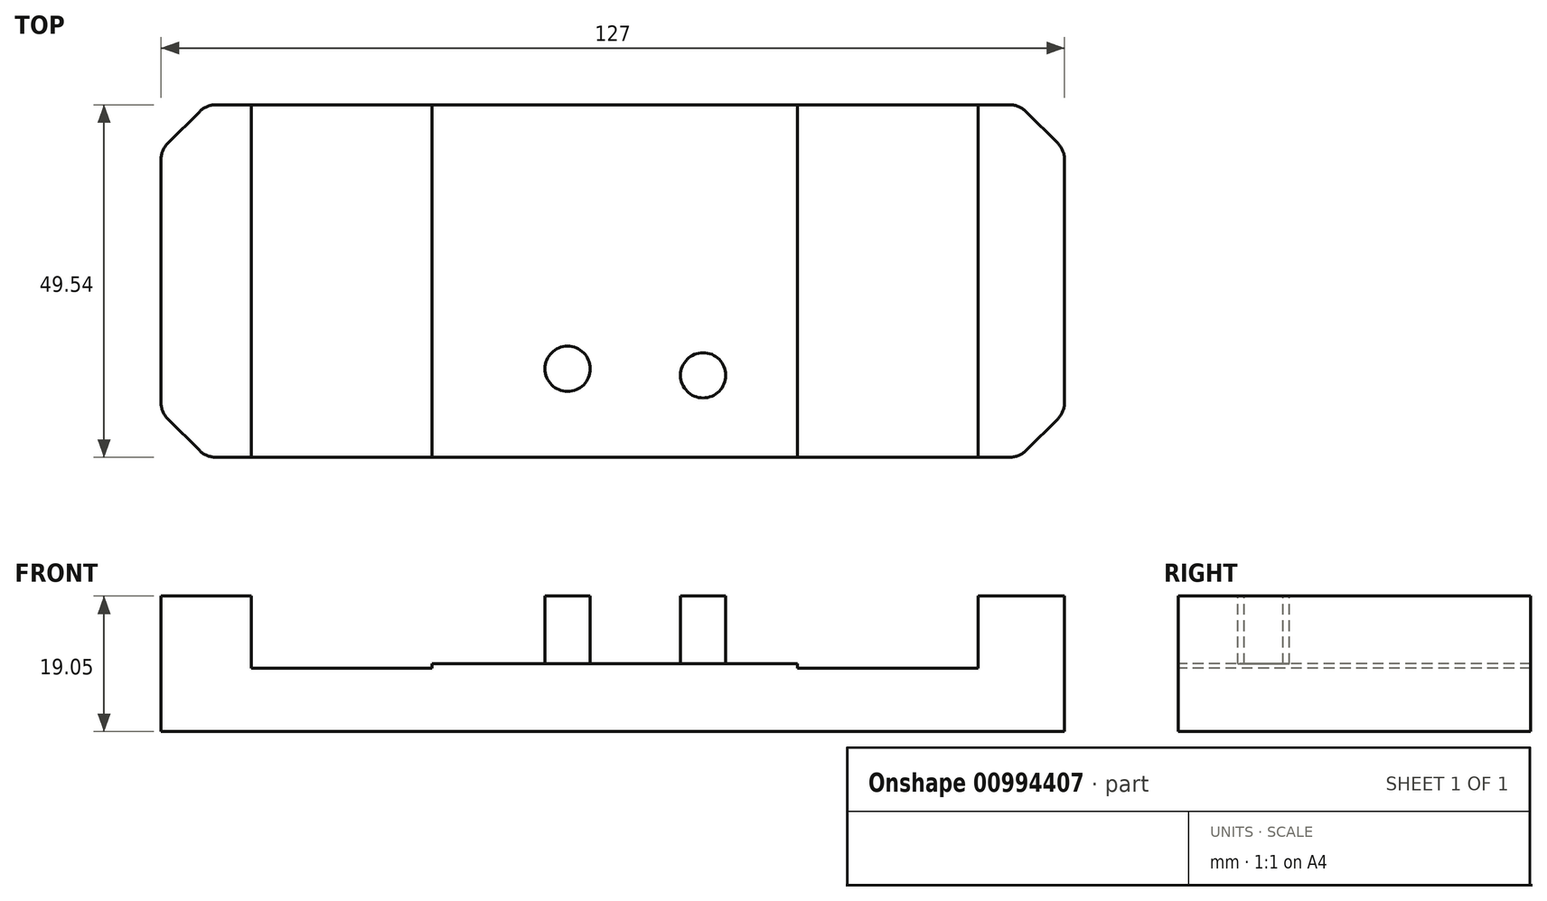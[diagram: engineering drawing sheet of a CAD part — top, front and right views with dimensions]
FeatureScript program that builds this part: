
annotation { "Feature Type Name" : "Feature", "Feature Type Description" : "" }
export const myFeature = defineFeature(function(context is Context, id is Id, definition is map)
    precondition{}
    {
        {
            var Q0;
            Q0=qCreatedBy(makeId("Top.planeOp"),FACE);
            var sketch = newSketch(context, id + "F0", { "sketchPlane" : qUnion([Q0])});
            skLineSegment(sketch, "E0.bottom", {"start": v(63.5, 24.77) * mm, "end": v(-63.5, 24.77) * mm});
            skLineSegment(sketch, "E0.top", {"start": v(63.5, -24.77) * mm, "end": v(-63.5, -24.77) * mm});
            skLineSegment(sketch, "E0.left", {"start": v(63.5, 24.77) * mm, "end": v(63.5, -24.76) * mm});
            skLineSegment(sketch, "E0.right", {"start": v(-63.5, 24.77) * mm, "end": v(-63.5, -24.77) * mm});
            skPoint(sketch, "E0.middle", {"position": v(0, 0) * mm});
            skSolve(sketch);
        }
        {
            var Q0;
            Q0=makeQuery(id+"F0.imprint","IMPRINT",FACE,{"disambiguationData":[TD([[makeQuery(id+"F0.imprint","IMPRINT",EDGE,{"derivedFrom":sQuery(id+"F0.wireOp",EDGE,"E0.bottom")}),1.0]])]});
            extrude(context, id + "F1", {"entities" : qUnion([Q0]), "depth" : 19.05 * mm, "offsetDistance" : 25.4 * mm});
        }
        {
            var Q0;
            Q0=makeQuery(id+"F1.opExtrude","CAP_FACE",FACE,{"disambiguationData":[OSD([sQuery(id+"F0.wireOp",EDGE,"E0.bottom"),sQuery(id+"F0.wireOp",EDGE,"E0.top"),sQuery(id+"F0.wireOp",EDGE,"E0.left"),sQuery(id+"F0.wireOp",EDGE,"E0.right")])],"isStart":false});
            var sketch = newSketch(context, id + "F2", { "sketchPlane" : qUnion([Q0])});
            skLineSegment(sketch, "E1.bottom", {"start": v(-50.8, 24.77) * mm, "end": v(-25.4, 24.77) * mm});
            skLineSegment(sketch, "E1.top", {"start": v(-50.8, -24.77) * mm, "end": v(-25.4, -24.77) * mm});
            skLineSegment(sketch, "E1.left", {"start": v(-50.8, 24.77) * mm, "end": v(-50.8, -24.77) * mm});
            skLineSegment(sketch, "E1.right", {"start": v(-25.4, 24.77) * mm, "end": v(-25.4, -24.77) * mm});
            skLineSegment(sketch, "E2", {"start": v(-63.5, 0) * mm, "end": v(63.5, 0) * mm, "construction": true});
            skCircle(sketch, "E3", {"center": v(-12.7, 0) * mm, "radius": 3.18 * mm});
            skCircle(sketch, "E4", {"center": v(15.88, 0) * mm, "radius": 3.18 * mm});
            skCircle(sketch, "E5", {"center": v(-6.35, 12.33) * mm, "radius": 3.18 * mm});
            skCircle(sketch, "E6", {"center": v(12.7, 13.24) * mm, "radius": 3.18 * mm});
            skCircle(sketch, "E7.MirrorC", {"center": v(-6.35, -12.33) * mm, "radius": 3.18 * mm});
            skCircle(sketch, "E8.MirrorC", {"center": v(12.7, -13.24) * mm, "radius": 3.18 * mm});
            skLineSegment(sketch, "E9.bottom", {"start": v(51.35, 24.77) * mm, "end": v(25.95, 24.77) * mm});
            skLineSegment(sketch, "E9.top", {"start": v(51.35, -24.77) * mm, "end": v(25.95, -24.77) * mm});
            skLineSegment(sketch, "E9.left", {"start": v(51.35, 24.77) * mm, "end": v(51.35, -24.77) * mm});
            skLineSegment(sketch, "E9.right", {"start": v(25.95, 24.77) * mm, "end": v(25.95, -24.77) * mm});
            skSolve(sketch);
        }
        {
            var Q0;
            Q0=makeQuery(id+"F2.imprint","IMPRINT",FACE,{"disambiguationData":[TD([[makeQuery(id+"F2.imprint","IMPRINT",EDGE,{"derivedFrom":sQuery(id+"F2.wireOp",EDGE,"E1.bottom")}),1.0]])]});
            extrude(context, id + "F3", {"entities" : qUnion([Q0]), "operationType" : NewBodyOperationType.REMOVE, "oppositeDirection" : true, "depth" : 10.16 * mm, "offsetDistance" : 25.4 * mm});
        }
        {
            var Q0;
            Q0=makeQuery(id+"F2.imprint","IMPRINT",FACE,{"disambiguationData":[TD([[makeQuery(id+"F2.imprint","IMPRINT",EDGE,{"derivedFrom":sQuery(id+"F2.wireOp",EDGE,"E9.bottom")}),1.0]])]});
            extrude(context, id + "F4", {"entities" : qUnion([Q0]), "operationType" : NewBodyOperationType.REMOVE, "oppositeDirection" : true, "depth" : 10.16 * mm, "offsetDistance" : 25.4 * mm});
        }
        {
            var Q0;
            Q0=makeQuery(id+"F2.imprint","IMPRINT",FACE,{"disambiguationData":[TD([[makeQuery(id+"F2.imprint","IMPRINT",EDGE,{"derivedFrom":sQuery(id+"F2.wireOp",EDGE,"E7.MirrorC")}),-1.0]])]});
            var Q1;
            Q1=makeQuery(id+"F2.imprint","IMPRINT",FACE,{"disambiguationData":[TD([[makeQuery(id+"F2.imprint","IMPRINT",EDGE,{"derivedFrom":sQuery(id+"F2.wireOp",EDGE,"E3")}),1.0]])]});
            var Q2;
            Q2=makeQuery(id+"F2.imprint","IMPRINT",FACE,{"disambiguationData":[TD([[makeQuery(id+"F2.imprint","IMPRINT",EDGE,{"derivedFrom":sQuery(id+"F2.wireOp",EDGE,"E5")}),1.0]])]});
            var Q3;
            Q3=makeQuery(id+"F2.imprint","IMPRINT",FACE,{"disambiguationData":[TD([[makeQuery(id+"F2.imprint","IMPRINT",EDGE,{"derivedFrom":sQuery(id+"F2.wireOp",EDGE,"E6")}),1.0]])]});
            var Q4;
            Q4=makeQuery(id+"F2.imprint","IMPRINT",FACE,{"disambiguationData":[TD([[makeQuery(id+"F2.imprint","IMPRINT",EDGE,{"derivedFrom":sQuery(id+"F2.wireOp",EDGE,"E4")}),1.0]])]});
            var Q5;
            Q5=makeQuery(id+"F2.imprint","IMPRINT",FACE,{"disambiguationData":[TD([[makeQuery(id+"F2.imprint","IMPRINT",EDGE,{"derivedFrom":sQuery(id+"F2.wireOp",EDGE,"E8.MirrorC")}),-1.0]])]});
            extrude(context, id + "F5", {"entities" : qUnion([Q0, Q1, Q2, Q3, Q4, Q5]), "operationType" : NewBodyOperationType.REMOVE, "oppositeDirection" : true, "depth" : 9.52 * mm, "offsetDistance" : 25.4 * mm});
        }
        {
            var Q0;
            Q0=makeQuery(id+"F1.opExtrude","SWEPT_EDGE",EDGE,{"disambiguationData":[OSD([sQuery(id+"F0.wireOp",EDGE,"E0.top"),sQuery(id+"F0.wireOp",EDGE,"E0.left")])]});
            var Q1;
            Q1=makeQuery(id+"F1.opExtrude","SWEPT_EDGE",EDGE,{"disambiguationData":[OSD([sQuery(id+"F0.wireOp",EDGE,"E0.bottom"),sQuery(id+"F0.wireOp",EDGE,"E0.left")])]});
            var Q2;
            Q2=makeQuery(id+"F1.opExtrude","SWEPT_EDGE",EDGE,{"disambiguationData":[OSD([sQuery(id+"F0.wireOp",EDGE,"E0.top"),sQuery(id+"F0.wireOp",EDGE,"E0.right")])]});
            var Q3;
            Q3=makeQuery(id+"F1.opExtrude","SWEPT_EDGE",EDGE,{"disambiguationData":[OSD([sQuery(id+"F0.wireOp",EDGE,"E0.bottom"),sQuery(id+"F0.wireOp",EDGE,"E0.right")])]});
            chamfer(context, id + "F6", {"entities" : qUnion([Q0, Q1, Q2, Q3]), "width" : 6.35 * mm, "tangentPropagation" : true});
        }
        {
            var Q0;
            {var subQ0=sQuery(id+"F0.wireOp",EDGE,"E0.top");Q0=makeQuery(id+"F6.opChamfer","BLEND_EDGE",EDGE,{"blendedFrom":[makeQuery(id+"F1.opExtrude","SWEPT_EDGE",EDGE,{"disambiguationData":[OSD([subQ0,sQuery(id+"F0.wireOp",EDGE,"E0.right")])]}),makeQuery(id+"F1.opExtrude","SWEPT_FACE",FACE,{"disambiguationData":[OSD([subQ0])]})],"blendedInto":[makeQuery(id+"F1.opExtrude","SWEPT_FACE",FACE,{"disambiguationData":[OSD([subQ0])]})]});}
            var Q1;
            {var subQ0=sQuery(id+"F0.wireOp",EDGE,"E0.top");Q1=makeQuery(id+"F6.opChamfer","BLEND_EDGE",EDGE,{"blendedFrom":[makeQuery(id+"F1.opExtrude","SWEPT_EDGE",EDGE,{"disambiguationData":[OSD([subQ0,sQuery(id+"F0.wireOp",EDGE,"E0.left")])]}),makeQuery(id+"F1.opExtrude","SWEPT_FACE",FACE,{"disambiguationData":[OSD([subQ0])]})],"blendedInto":[makeQuery(id+"F1.opExtrude","SWEPT_FACE",FACE,{"disambiguationData":[OSD([subQ0])]})]});}
            var Q2;
            {var subQ0=sQuery(id+"F0.wireOp",EDGE,"E0.left");Q2=makeQuery(id+"F6.opChamfer","BLEND_EDGE",EDGE,{"blendedFrom":[makeQuery(id+"F1.opExtrude","SWEPT_EDGE",EDGE,{"disambiguationData":[OSD([sQuery(id+"F0.wireOp",EDGE,"E0.top"),subQ0])]}),makeQuery(id+"F1.opExtrude","SWEPT_FACE",FACE,{"disambiguationData":[OSD([subQ0])]})],"blendedInto":[makeQuery(id+"F1.opExtrude","SWEPT_FACE",FACE,{"disambiguationData":[OSD([subQ0])]})]});}
            var Q3;
            {var subQ0=sQuery(id+"F0.wireOp",EDGE,"E0.left");Q3=makeQuery(id+"F6.opChamfer","BLEND_EDGE",EDGE,{"blendedFrom":[makeQuery(id+"F1.opExtrude","SWEPT_EDGE",EDGE,{"disambiguationData":[OSD([sQuery(id+"F0.wireOp",EDGE,"E0.bottom"),subQ0])]}),makeQuery(id+"F1.opExtrude","SWEPT_FACE",FACE,{"disambiguationData":[OSD([subQ0])]})],"blendedInto":[makeQuery(id+"F1.opExtrude","SWEPT_FACE",FACE,{"disambiguationData":[OSD([subQ0])]})]});}
            var Q4;
            {var subQ0=sQuery(id+"F0.wireOp",EDGE,"E0.right");Q4=makeQuery(id+"F6.opChamfer","BLEND_EDGE",EDGE,{"blendedFrom":[makeQuery(id+"F1.opExtrude","SWEPT_EDGE",EDGE,{"disambiguationData":[OSD([sQuery(id+"F0.wireOp",EDGE,"E0.top"),subQ0])]}),makeQuery(id+"F1.opExtrude","SWEPT_FACE",FACE,{"disambiguationData":[OSD([subQ0])]})],"blendedInto":[makeQuery(id+"F1.opExtrude","SWEPT_FACE",FACE,{"disambiguationData":[OSD([subQ0])]})]});}
            var Q5;
            {var subQ0=sQuery(id+"F0.wireOp",EDGE,"E0.bottom");Q5=makeQuery(id+"F6.opChamfer","BLEND_EDGE",EDGE,{"blendedFrom":[makeQuery(id+"F1.opExtrude","SWEPT_EDGE",EDGE,{"disambiguationData":[OSD([subQ0,sQuery(id+"F0.wireOp",EDGE,"E0.left")])]}),makeQuery(id+"F1.opExtrude","SWEPT_FACE",FACE,{"disambiguationData":[OSD([subQ0])]})],"blendedInto":[makeQuery(id+"F1.opExtrude","SWEPT_FACE",FACE,{"disambiguationData":[OSD([subQ0])]})]});}
            var Q6;
            {var subQ0=sQuery(id+"F0.wireOp",EDGE,"E0.bottom");Q6=makeQuery(id+"F6.opChamfer","BLEND_EDGE",EDGE,{"blendedFrom":[makeQuery(id+"F1.opExtrude","SWEPT_EDGE",EDGE,{"disambiguationData":[OSD([subQ0,sQuery(id+"F0.wireOp",EDGE,"E0.right")])]}),makeQuery(id+"F1.opExtrude","SWEPT_FACE",FACE,{"disambiguationData":[OSD([subQ0])]})],"blendedInto":[makeQuery(id+"F1.opExtrude","SWEPT_FACE",FACE,{"disambiguationData":[OSD([subQ0])]})]});}
            var Q7;
            {var subQ0=sQuery(id+"F0.wireOp",EDGE,"E0.right");Q7=makeQuery(id+"F6.opChamfer","BLEND_EDGE",EDGE,{"blendedFrom":[makeQuery(id+"F1.opExtrude","SWEPT_EDGE",EDGE,{"disambiguationData":[OSD([sQuery(id+"F0.wireOp",EDGE,"E0.bottom"),subQ0])]}),makeQuery(id+"F1.opExtrude","SWEPT_FACE",FACE,{"disambiguationData":[OSD([subQ0])]})],"blendedInto":[makeQuery(id+"F1.opExtrude","SWEPT_FACE",FACE,{"disambiguationData":[OSD([subQ0])]})]});}
            fillet(context, id + "F7", {"entities" : qUnion([Q0, Q1, Q2, Q3, Q4, Q5, Q6, Q7]), "radius" : 3.17 * mm, "tangentPropagation" : true, "allowEdgeOverflow" : false});
        }
    });
